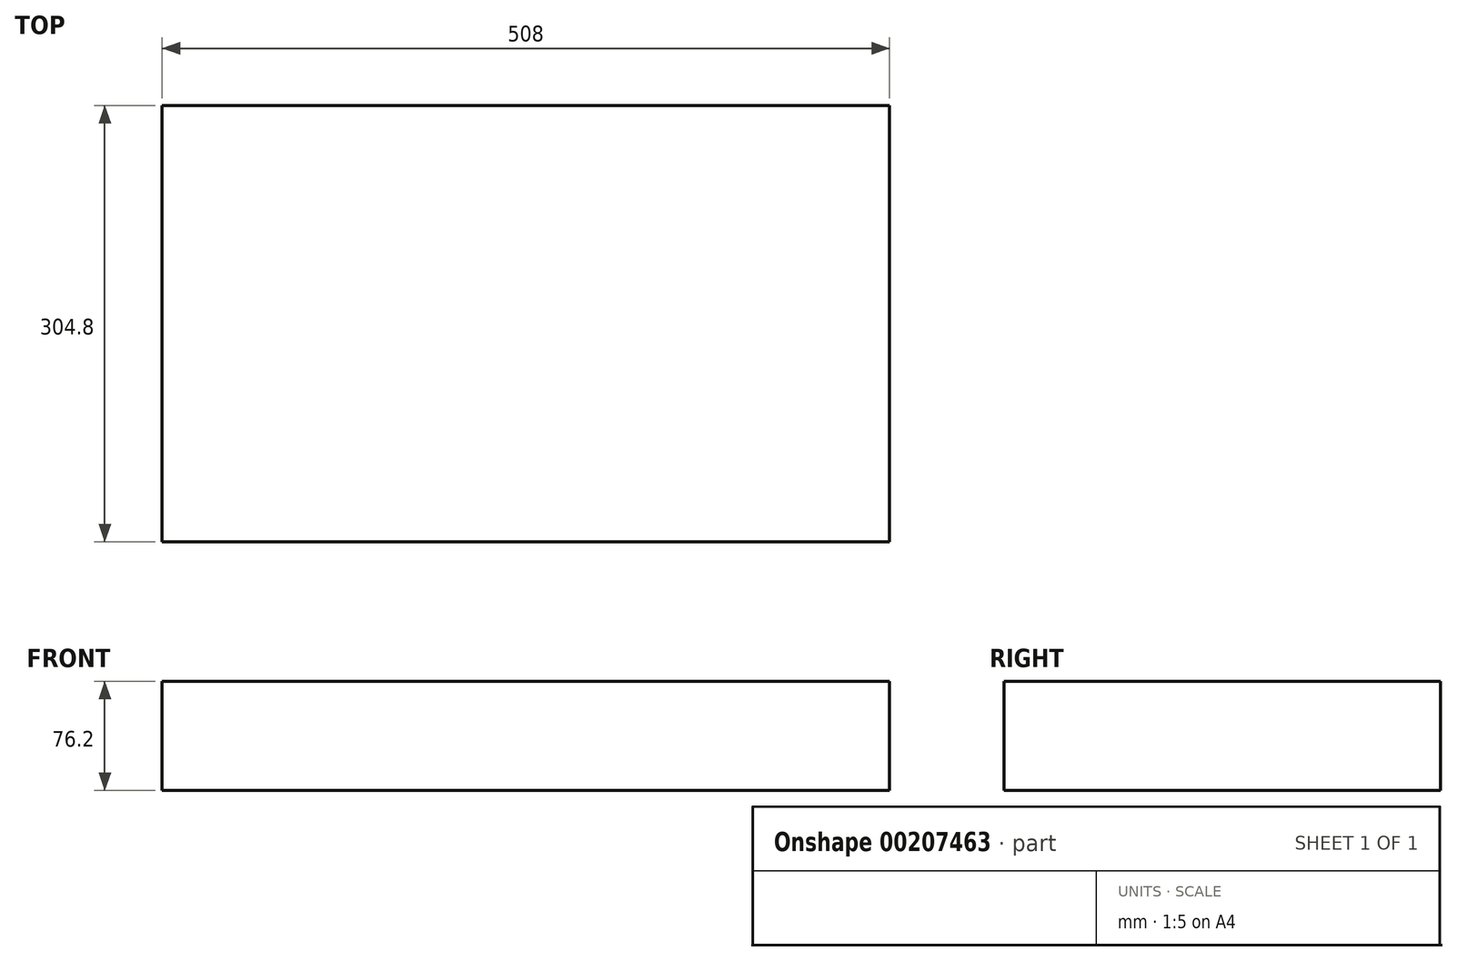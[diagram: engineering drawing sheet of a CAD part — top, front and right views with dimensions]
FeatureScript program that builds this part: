
annotation { "Feature Type Name" : "Feature", "Feature Type Description" : "" }
export const myFeature = defineFeature(function(context is Context, id is Id, definition is map)
    precondition{}
    {
        {
            var Q0;
            Q0=qCreatedBy(makeId("Top.planeOp"),FACE);
            var sketch = newSketch(context, id + "F0", { "sketchPlane" : qUnion([Q0])});
            skLineSegment(sketch, "E0.bottom", {"start": v(254, -152.4) * mm, "end": v(-254, -152.4) * mm});
            skLineSegment(sketch, "E0.top", {"start": v(254, 152.4) * mm, "end": v(-254, 152.4) * mm});
            skLineSegment(sketch, "E0.left", {"start": v(254, -152.4) * mm, "end": v(254, 152.4) * mm});
            skLineSegment(sketch, "E0.right", {"start": v(-254, -152.4) * mm, "end": v(-254, 152.4) * mm});
            skPoint(sketch, "E0.middle", {"position": v(0, 0) * mm});
            skSolve(sketch);
        }
        {
            var Q0;
            Q0 = qSketchRegion(id + "F0", true);
            extrude(context, id + "F1", {"entities" : qUnion([Q0]), "depth" : 76.2 * mm});
        }
    });
